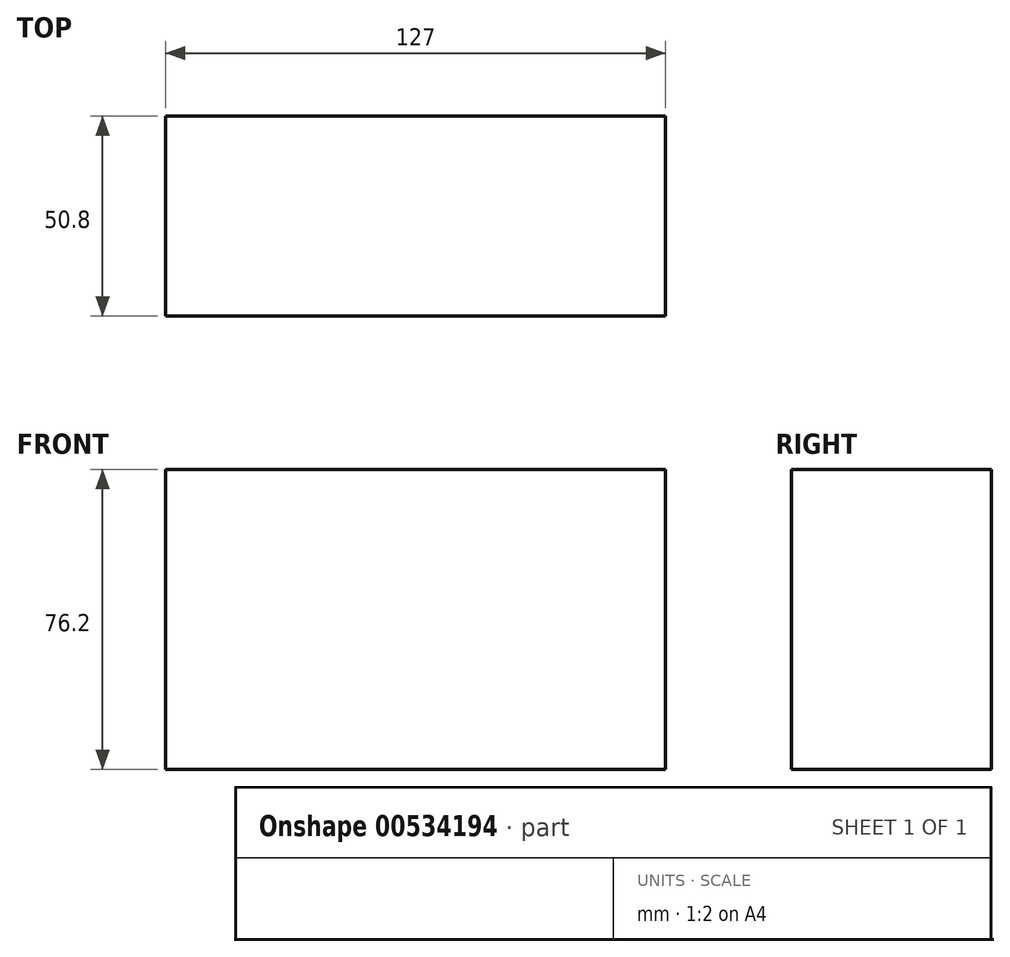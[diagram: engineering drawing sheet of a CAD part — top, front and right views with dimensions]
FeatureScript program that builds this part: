
annotation { "Feature Type Name" : "Feature", "Feature Type Description" : "" }
export const myFeature = defineFeature(function(context is Context, id is Id, definition is map)
    precondition{}
    {
        {
            var Q0;
            Q0=qCreatedBy(makeId("Front.planeOp"),FACE);
            var sketch = newSketch(context, id + "F0", { "sketchPlane" : qUnion([Q0])});
            skLineSegment(sketch, "E0", {"start": v(-63.49, 25.56) * mm, "end": v(-63.49, -50.64) * mm});
            skLineSegment(sketch, "E1", {"start": v(-63.49, -50.64) * mm, "end": v(63.51, -50.64) * mm});
            skLineSegment(sketch, "E2", {"start": v(63.51, -50.64) * mm, "end": v(63.51, 25.56) * mm});
            skLineSegment(sketch, "E3", {"start": v(63.51, 25.56) * mm, "end": v(-63.49, 25.56) * mm});
            skSolve(sketch);
        }
        {
            var Q0;
            Q0 = qSketchRegion(id + "F0", true);
            extrude(context, id + "F1", {"entities" : qUnion([Q0]), "depth" : 50.8 * mm, "offsetDistance" : 25.4 * mm});
        }
    });
